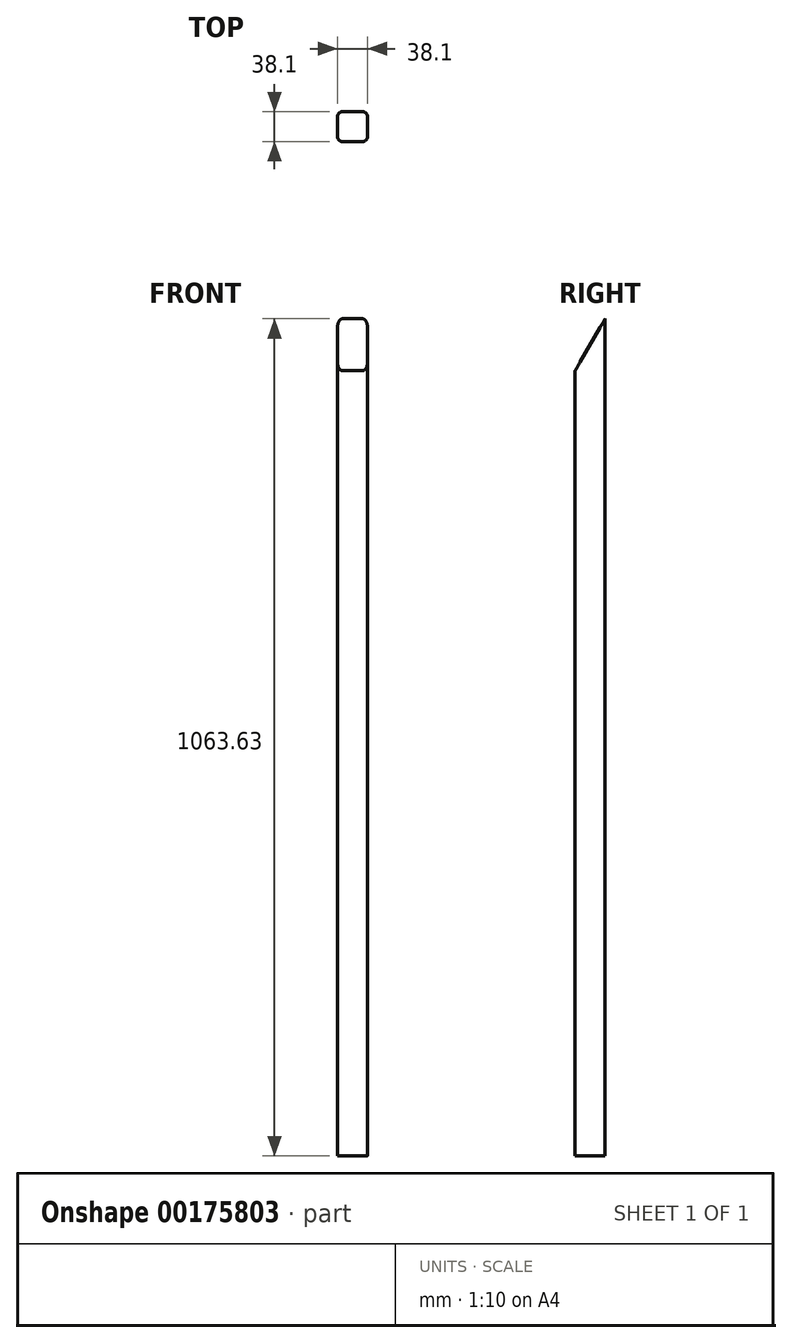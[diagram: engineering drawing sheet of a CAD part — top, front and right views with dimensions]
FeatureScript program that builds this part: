
annotation { "Feature Type Name" : "Feature", "Feature Type Description" : "" }
export const myFeature = defineFeature(function(context is Context, id is Id, definition is map)
    precondition{}
    {
        {
            var Q0;
            Q0=qCreatedBy(makeId("Top.planeOp"),FACE);
            var sketch = newSketch(context, id + "F0", { "sketchPlane" : qUnion([Q0])});
            skLineSegment(sketch, "E0.bottom", {"start": v(12.7, 19.05) * mm, "end": v(-12.7, 19.05) * mm});
            skLineSegment(sketch, "E0.top", {"start": v(12.7, -19.05) * mm, "end": v(-12.7, -19.05) * mm});
            skLineSegment(sketch, "E0.left", {"start": v(19.05, 12.7) * mm, "end": v(19.05, -12.7) * mm});
            skLineSegment(sketch, "E0.right", {"start": v(-19.05, 12.7) * mm, "end": v(-19.05, -12.7) * mm});
            skPoint(sketch, "E0.middle", {"position": v(0, 0) * mm});
            skPoint(sketch, "E1.visualSharp", {"position": v(-19.05, 19.05) * mm});
            skArc(sketch, "E1.filletArc", {"start": v(-12.7, 19.05) * mm, "mid": v(-17.2, 17.2) * mm, "end": v(-19.05, 12.7) * mm});
            skPoint(sketch, "E2.visualSharp", {"position": v(19.05, 19.05) * mm});
            skArc(sketch, "E2.filletArc", {"start": v(19.05, 12.7) * mm, "mid": v(17.2, 17.2) * mm, "end": v(12.7, 19.05) * mm});
            skPoint(sketch, "E3.visualSharp", {"position": v(19.05, -19.05) * mm});
            skArc(sketch, "E3.filletArc", {"start": v(12.7, -19.05) * mm, "mid": v(17.2, -17.2) * mm, "end": v(19.05, -12.7) * mm});
            skPoint(sketch, "E4.visualSharp", {"position": v(-19.05, -19.05) * mm});
            skArc(sketch, "E4.filletArc", {"start": v(-19.05, -12.7) * mm, "mid": v(-17.2, -17.2) * mm, "end": v(-12.7, -19.05) * mm});
            skSolve(sketch);
        }
        {
            var Q0;
            Q0=qSketchRegion(id+"F0",true);
            extrude(context, id + "F1", {"entities" : qUnion([Q0]), "depth" : 1063.62 * mm, "offsetDistance" : 25.4 * mm});
        }
        {
            var Q0;
            Q0=makeQuery(id+"F1.opExtrude","SWEPT_FACE",FACE,{"disambiguationData":[OSD([sQuery(id+"F0.wireOp",EDGE,"E0.right")])]});
            var sketch = newSketch(context, id + "F2", { "sketchPlane" : qUnion([Q0])});
            skLineSegment(sketch, "E5", {"start": v(-19.05, 1063.62) * mm, "end": v(19.05, 997.63) * mm});
            skPoint(sketch, "E5.startSnap0", {"position": v(0, 1063.62) * mm});
            skLineSegment(sketch, "E6", {"start": v(19.05, 997.63) * mm, "end": v(19.05, 1063.62) * mm});
            skLineSegment(sketch, "E7", {"start": v(19.05, 1063.62) * mm, "end": v(-19.05, 1063.62) * mm});
            skSolve(sketch);
        }
        {
            var Q0;
            {var subQ0=sQuery(id+"F2.wireOp",EDGE,"E6");Q0=makeQuery(id+"F2.imprint","IMPRINT",FACE,{"disambiguationData":[TD([[makeQuery(id+"F2.imprint","IMPRINT",EDGE,{"derivedFrom":subQ0}),1.0]])]});}
            var Q1;
            {var subQ0=sQuery(id+"F2.wireOp",EDGE,"E5");var subQ1=sQuery(id+"F0.wireOp",EDGE,"E0.right");var subQ2=makeQuery(id+"F1.opExtrude","SWEPT_EDGE",EDGE,{"disambiguationData":[OSD([subQ1,sQuery(id+"F0.wireOp",EDGE,"E1.filletArc")])]});var subQ3=makeQuery(id+"F2.imprint","INTERSECT",VERTEX,{"derivedFrom":[subQ2,subQ0]});Q1=makeQuery(id+"F2.imprint","IMPRINT",FACE,{"disambiguationData":[TD([[makeQuery(id+"F2.imprint","IMPRINT",EDGE,{"disambiguationData":[TD([[subQ3,-1.0]])],"derivedFrom":subQ0}),1.0]])]});}
            var Q2;
            {var subQ0=sQuery(id+"F2.wireOp",EDGE,"E7");var subQ1=sQuery(id+"F2.wireOp",EDGE,"E5");var subQ2=makeQuery(id+"F2.imprint","INTERSECT",VERTEX,{"derivedFrom":[subQ1,subQ0]});Q2=makeQuery(id+"F2.imprint","IMPRINT",FACE,{"disambiguationData":[TD([[makeQuery(id+"F2.imprint","IMPRINT",EDGE,{"disambiguationData":[TD([[subQ2,-1.0]])],"derivedFrom":subQ1}),1.0]])]});}
            extrude(context, id + "F3", {"entities" : qUnion([Q0, Q1, Q2]), "operationType" : NewBodyOperationType.REMOVE, "oppositeDirection" : true, "depth" : 38.1 * mm, "offsetDistance" : 25.4 * mm});
        }
    });
